# Revit family: Theatre-Equipment_Wenger-Strata--
name_source: partatom
category: Specialty Equipment
revit_build: Autodesk Revit 2018 (Build: 20190510_1515(x64)
units: mm (PartAtom-declared; Revit-internal decimal feet)

## family parameters
Always vertical = Yes
Cut with Voids When Loaded = No
OmniClass Number = 23.21.25.11.17.11
Part Type = Normal
Room Calculation Point = No
Round Connector Dimension = Use Radius
Shared = No
Work Plane-Based = No

## types (1)
- Standard
    Assembly Code = E1020300
    Deck Material = <By Category>
    Description = Orchestra Pit Filler
    ENGworks URL = http://www.ENGworks.com
    Framing Component Material = Metal - Wenger - Aluminum
    Manufacturer = Wenger
    Model = 182A000
    Product Page URL = https://www.wengercorp.com
    Series = STRATA®
    Standards = System meets building code standards of L/360; Standard system meets a vertical live load of 150 psf
    URL = https://www.wengercorp.com
    Version = 1
    【︎Brace】 Bottom Offset = 1' - 11 1/4"
    【︎Brace】 Center Offset = 1' - 8 1/4"
    【︎Brace】 Length = 2' - 2 3/4"
    【︎Brace】Top Offset = 1' - 5 1/4"
    【︎Deck】 Overhang Offset = 0' - 6"
    【︎Deck】 Thickness = 0' - 3 9/16"
    【︎Main Beam】 Back Offset = 1' - 0"
    【︎Main Beam】 Front Offset = 0' - 9"
    【︎Main Beam】 Height = 0' - 6"
    【︎Main Beam】 Joint Offset = 0' - 2 1/2"

## geometry (parser evidence)
native form markers: Sweep x21
no freeform markers — native parametric forms only
